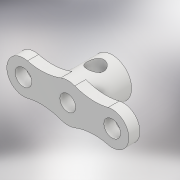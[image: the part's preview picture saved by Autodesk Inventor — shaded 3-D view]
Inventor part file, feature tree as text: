
AUTODESK INVENTOR PART (.ipt)
format: ipt  version: 2018.2 (Build 222227000, 227)  size: 166,400 bytes
history: native  units: mm
features: extrude x3, sketch x2, plane x1
ambient origin geometry x8: Origin, YZ Plane, XZ Plane, XY Plane, X Axis, Y Axis, Z Axis, Center Point
bodies: Solid1 (feature_tree)
feature tree (6):
  sketch  "Sketch1"  dims[d0=2.85mm d1=7.0mm]
  extrude  "Extrusion1"  Depth=7.0mm
  extrude  "Extrusion2"  Depth=3.0mm
  extrude  "Extrusion3"  Depth=10.0mm
  plane  "Work Plane1"
  sketch  "Sketch2"  dims[d2=3.0mm d3=3.0mm d4=8.0mm d5=8.0mm d6=3.0mm d7=2.0mm d8=0.0mm d9=6.0mm d10=0.0mm d11=3.0mm d12=6.0mm d13=0.0mm d14=10.0mm]
